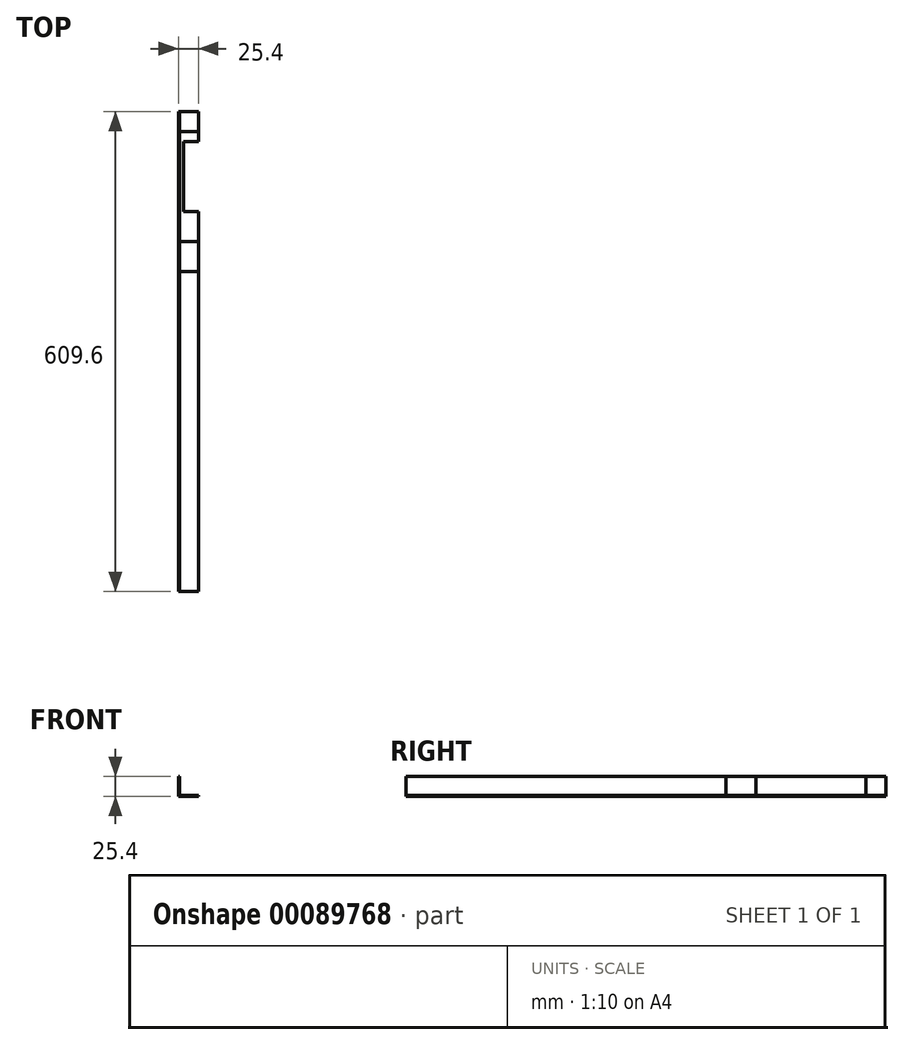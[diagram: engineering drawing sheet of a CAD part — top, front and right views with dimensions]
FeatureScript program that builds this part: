
annotation { "Feature Type Name" : "Feature", "Feature Type Description" : "" }
export const myFeature = defineFeature(function(context is Context, id is Id, definition is map)
    precondition{}
    {
        {
            var Q0;
            Q0=qCreatedBy(makeId("Front.planeOp"),FACE);
            var sketch = newSketch(context, id + "F0", { "sketchPlane" : qUnion([Q0])});
            skLineSegment(sketch, "E0", {"start": v(0, 0) * mm, "end": v(0, 25.4) * mm});
            skLineSegment(sketch, "E1", {"start": v(0, 25.4) * mm, "end": v(1.59, 25.4) * mm});
            skLineSegment(sketch, "E2", {"start": v(1.59, 25.4) * mm, "end": v(1.59, 1.59) * mm});
            skLineSegment(sketch, "E3", {"start": v(1.59, 1.59) * mm, "end": v(25.4, 1.59) * mm});
            skLineSegment(sketch, "E4", {"start": v(25.4, 1.59) * mm, "end": v(25.4, 0) * mm});
            skLineSegment(sketch, "E5", {"start": v(25.4, 0) * mm, "end": v(0, 0) * mm});
            skSolve(sketch);
        }
        {
            var Q0;
            Q0=makeQuery(id+"F0.imprint","IMPRINT",FACE,{"disambiguationData":[TD([[makeQuery(id+"F0.imprint","IMPRINT",EDGE,{"derivedFrom":sQuery(id+"F0.wireOp",EDGE,"E0")}),-1.0]])]});
            extrude(context, id + "F1", {"entities" : qUnion([Q0]), "depth" : 203.2 * mm});
        }
        {
            var Q0;
            Q0=qSketchRegion(id+"F0",true);
            extrude(context, id + "F2", {"entities" : qUnion([Q0]), "depth" : 609.6 * mm});
        }
        {
            var Q0;
            Q0=qSketchRegion(id+"F0",true);
            extrude(context, id + "F3", {"entities" : qUnion([Q0]), "depth" : 25.4 * mm});
        }
        {
            var Q0;
            Q0=qSketchRegion(id+"F0",true);
            extrude(context, id + "F4", {"entities" : qUnion([Q0]), "depth" : 165.1 * mm});
        }
        {
            var Q0;
            Q0=makeQuery(id+"F4.opExtrude","SWEPT_FACE",FACE,{"disambiguationData":[OSD([sQuery(id+"F0.wireOp",EDGE,"E3")])]});
            var sketch = newSketch(context, id + "F5", { "sketchPlane" : qUnion([Q0])});
            skLineSegment(sketch, "E6", {"start": v(25.4, -38.1) * mm, "end": v(6.35, -38.1) * mm});
            skLineSegment(sketch, "E7", {"start": v(6.35, -38.1) * mm, "end": v(6.35, -127) * mm});
            skLineSegment(sketch, "E8", {"start": v(6.35, -127) * mm, "end": v(25.4, -127) * mm});
            skLineSegment(sketch, "E9", {"start": v(25.4, -38.1) * mm, "end": v(25.4, -127) * mm});
            skSolve(sketch);
        }
        {
            var Q0;
            Q0=makeQuery(id+"F5.imprint","IMPRINT",FACE,{"disambiguationData":[TD([[makeQuery(id+"F5.imprint","IMPRINT",EDGE,{"derivedFrom":sQuery(id+"F5.wireOp",EDGE,"E6")}),1.0]])]});
            extrude(context, id + "F6", {"entities" : qUnion([Q0]), "operationType" : NewBodyOperationType.REMOVE, "oppositeDirection" : true, "depth" : 25.4 * mm});
        }
        {
            var Q0;
            Q0=qSketchRegion(id+"F0",true);
            extrude(context, id + "F7", {"entities" : qUnion([Q0]), "depth" : 203.2 * mm});
        }
        {
            var Q0;
            Q0=makeQuery(id+"F7.opExtrude","SWEPT_BODY",BODY,{"disambiguationData":[OSD([sQuery(id+"F0.wireOp",EDGE,"E0"),sQuery(id+"F0.wireOp",EDGE,"E1"),sQuery(id+"F0.wireOp",EDGE,"E2"),sQuery(id+"F0.wireOp",EDGE,"E3"),sQuery(id+"F0.wireOp",EDGE,"E4"),sQuery(id+"F0.wireOp",EDGE,"E5")])]});
            deleteBodies(context, id + "F8", {"entities" : qUnion([Q0])});
        }
    });
